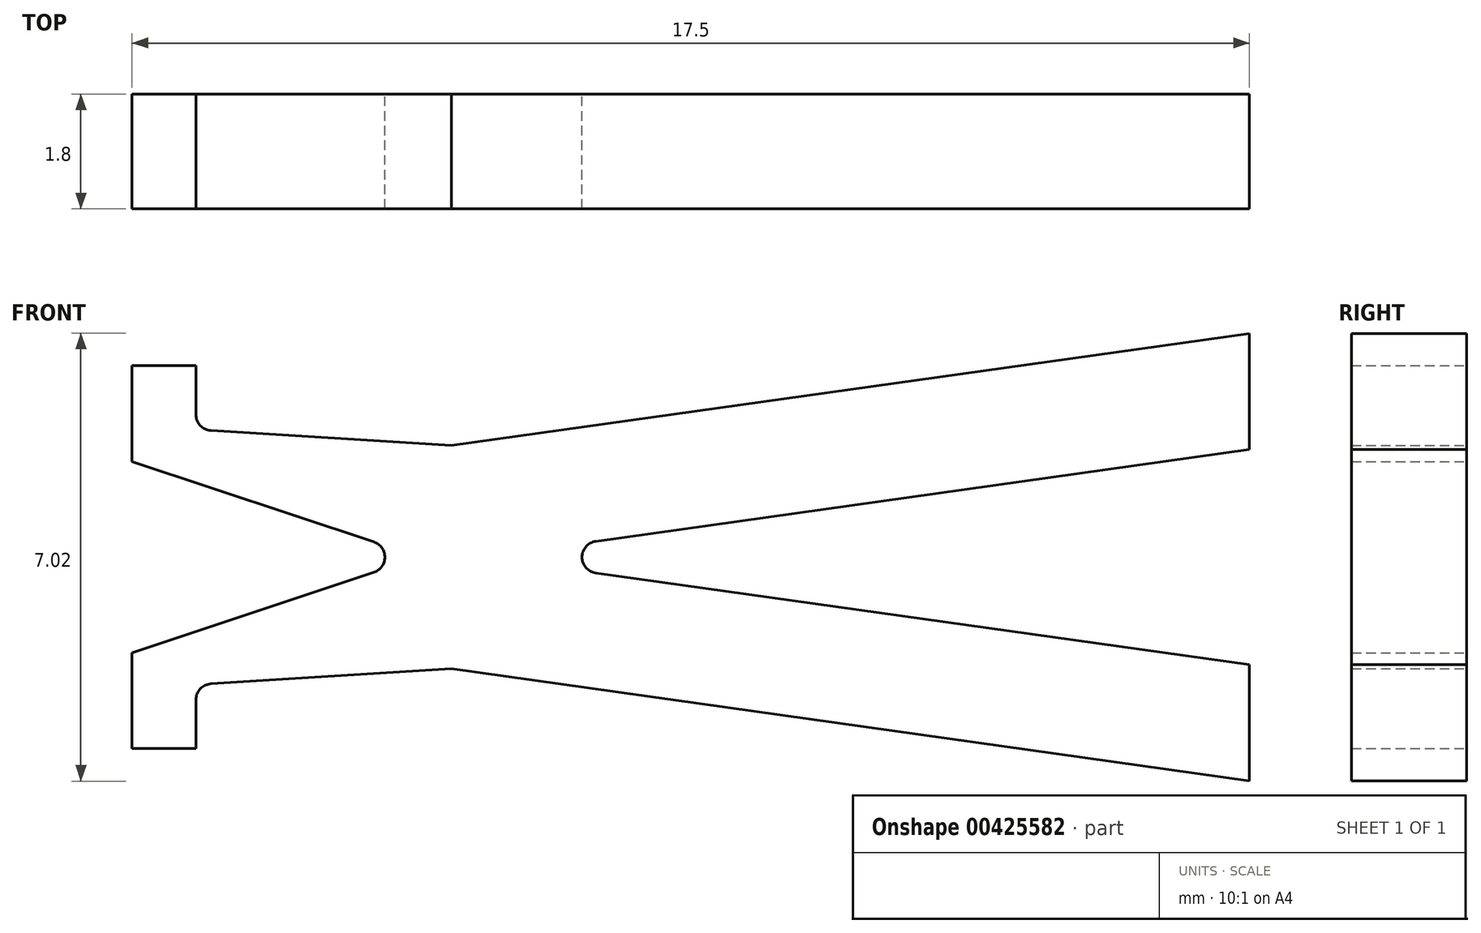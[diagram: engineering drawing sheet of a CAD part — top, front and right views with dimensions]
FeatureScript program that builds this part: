
annotation { "Feature Type Name" : "Feature", "Feature Type Description" : "" }
export const myFeature = defineFeature(function(context is Context, id is Id, definition is map)
    precondition{}
    {
        {
            var Q0;
            Q0=qCreatedBy(makeId("Front.planeOp"),FACE);
            var sketch = newSketch(context, id + "F0", { "sketchPlane" : qUnion([Q0])});
            skLineSegment(sketch, "E0", {"start": v(-4.5, 1.75) * mm, "end": v(8, 3.5) * mm});
            skLineSegment(sketch, "E1", {"start": v(8, 3.5) * mm, "end": v(8, 1.69) * mm});
            skLineSegment(sketch, "E2", {"start": v(8, 1.69) * mm, "end": v(-4, 0) * mm});
            skLineSegment(sketch, "E3", {"start": v(-9.5, 1.5) * mm, "end": v(-5, 0) * mm});
            skLineSegment(sketch, "E4", {"start": v(-9.5, 1.5) * mm, "end": v(-9.5, 3) * mm});
            skLineSegment(sketch, "E5", {"start": v(-9.5, 3) * mm, "end": v(-8.5, 3) * mm});
            skLineSegment(sketch, "E6", {"start": v(-8.5, 3) * mm, "end": v(-8.5, 2) * mm});
            skLineSegment(sketch, "E7", {"start": v(-8.5, 2) * mm, "end": v(-4.5, 1.75) * mm});
            skLineSegment(sketch, "E8", {"start": v(-5, 0) * mm, "end": v(-4, 0) * mm, "construction": true});
            skLineSegment(sketch, "E9.MirrorCS", {"start": v(8, -3.5) * mm, "end": v(8, -1.69) * mm});
            skLineSegment(sketch, "E10.MirrorCS", {"start": v(-4.5, -1.75) * mm, "end": v(8, -3.5) * mm});
            skLineSegment(sketch, "E11.MirrorCS", {"start": v(-9.5, -1.5) * mm, "end": v(-9.5, -3) * mm});
            skLineSegment(sketch, "E12.MirrorCS", {"start": v(-9.5, -3) * mm, "end": v(-8.5, -3) * mm});
            skLineSegment(sketch, "E13.MirrorCS", {"start": v(8, -1.69) * mm, "end": v(-4, 0) * mm});
            skLineSegment(sketch, "E14.MirrorCS", {"start": v(-8.5, -3) * mm, "end": v(-8.5, -2) * mm});
            skLineSegment(sketch, "E15.MirrorCS", {"start": v(-9.5, -1.5) * mm, "end": v(-5, 0) * mm});
            skLineSegment(sketch, "E16.MirrorCS", {"start": v(-8.5, -2) * mm, "end": v(-4.5, -1.75) * mm});
            skLineSegment(sketch, "E17", {"start": v(-4.5, 0) * mm, "end": v(-4.5, 1.75) * mm, "construction": true});
            skLineSegment(sketch, "E18", {"start": v(-9.5, 1.5) * mm, "end": v(-8.5, 3) * mm, "construction": true});
            skSolve(sketch);
        }
        {
            var Q0;
            Q0 = qSketchRegion(id + "F0", true);
            extrude(context, id + "F1", {"entities" : qUnion([Q0]), "depth" : 1.8 * mm});
        }
        {
            var Q0;
            Q0=makeQuery(id+"F1.opExtrude","SWEPT_EDGE",EDGE,{"disambiguationData":[OSD([sQuery(id+"F0.wireOp",EDGE,"E2"),sQuery(id+"F0.wireOp",EDGE,"E13.MirrorCS")])]});
            var Q1;
            Q1=makeQuery(id+"F1.opExtrude","SWEPT_EDGE",EDGE,{"disambiguationData":[OSD([sQuery(id+"F0.wireOp",EDGE,"E3"),sQuery(id+"F0.wireOp",EDGE,"E15.MirrorCS")])]});
            fillet(context, id + "F2", {"entities" : qUnion([Q0, Q1]), "radius" : .25 * mm, "tangentPropagation" : true, "allowEdgeOverflow" : false});
        }
        {
            var Q0;
            Q0=makeQuery(id+"F1.opExtrude","SWEPT_EDGE",EDGE,{"disambiguationData":[OSD([sQuery(id+"F0.wireOp",EDGE,"E6"),sQuery(id+"F0.wireOp",EDGE,"E7")])]});
            var Q1;
            Q1=makeQuery(id+"F1.opExtrude","SWEPT_EDGE",EDGE,{"disambiguationData":[OSD([sQuery(id+"F0.wireOp",EDGE,"E14.MirrorCS"),sQuery(id+"F0.wireOp",EDGE,"E16.MirrorCS")])]});
            fillet(context, id + "F3", {"entities" : qUnion([Q0, Q1]), "radius" : .25 * mm, "tangentPropagation" : true, "allowEdgeOverflow" : false});
        }
    });
